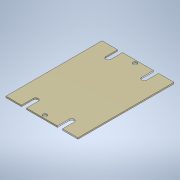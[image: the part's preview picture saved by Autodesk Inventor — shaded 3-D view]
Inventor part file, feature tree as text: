
AUTODESK INVENTOR PART (.ipt)
format: ipt  version: 2022 (Build 260153000, 153)  size: 185,344 bytes
history: native  units: in
note: dims shown in document units (in); Inventor stores cm internally (conversion verified against a paired STEP export)
features: sketch x3, extrude x2, hole x1
ambient origin geometry x8: Origin, YZ Plane, XZ Plane, XY Plane, X Axis, Y Axis, Z Axis, Center Point
bodies: Body1 (feature_tree)
feature tree (6):
  extrude  "Extrusion2"  Depth=2.2638in
  extrude  "Extrusion3"  Depth=0.1181in
  hole  "Hole1"  [1 undecoded]
  sketch  "Sketch2"  dims[d28=1.6969in d29=2.2638in]
  sketch  "Sketch3"  dims[d30=0.0315in d31=0.0in d32=0.1181in]
  sketch  "Sketch4"  dims[d33=0.2756in d34=0.0591in d35=0.0in d36=0.0in d37=0.8484in d38=0.0689in d40=0.0689in d41=0.0945in d42=0.1575in d43=0.1732in d44=0.0787in d45=0.6181in d46=0.315in d47=0.8108in d48=0.4242in]
note: 1 required parameter value undecoded (feature->parameter linkage not recoverable at this tier; creation-order binding heuristic only, values carry confidence <= 0.55)
